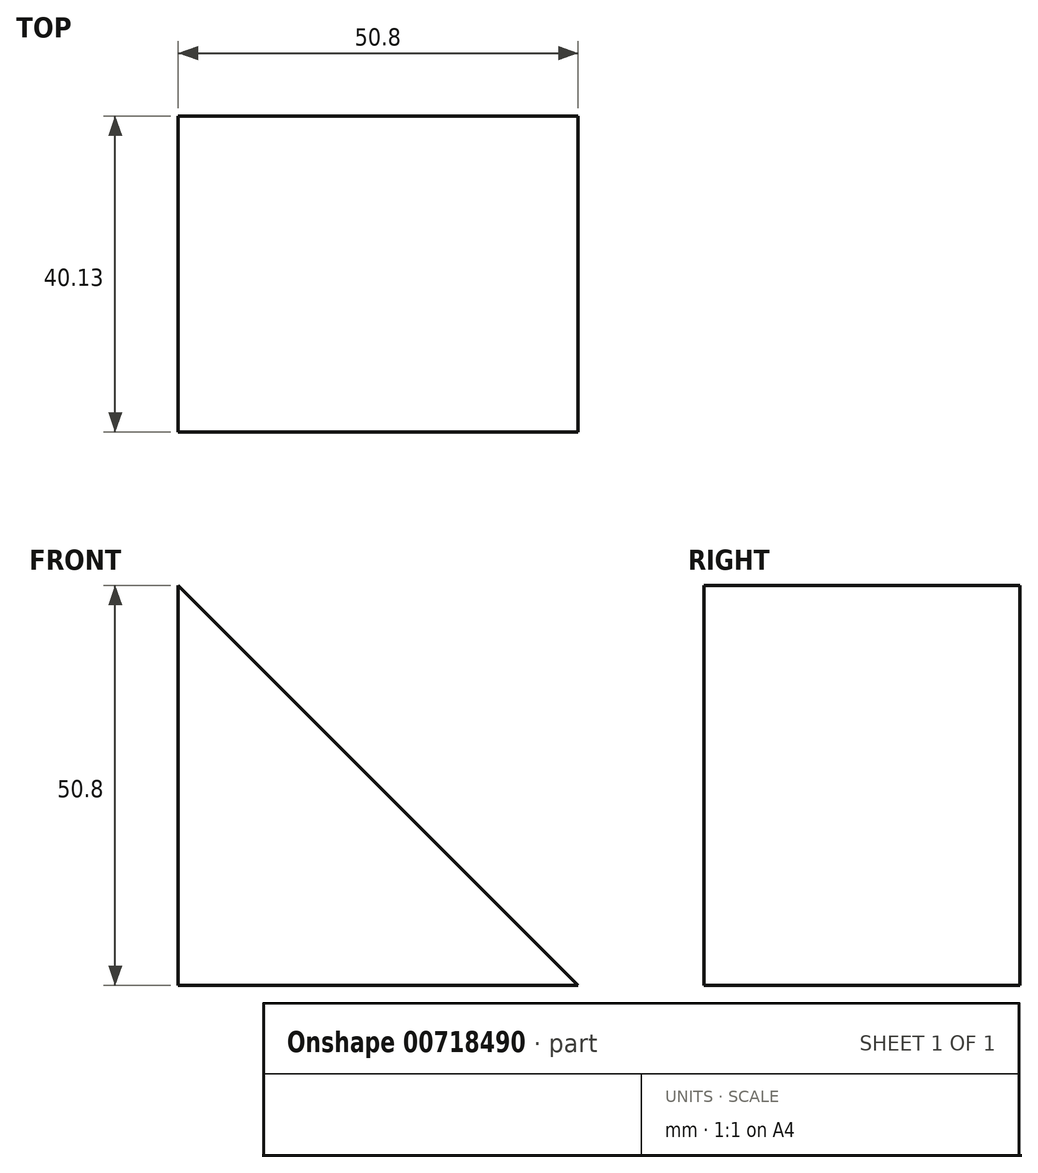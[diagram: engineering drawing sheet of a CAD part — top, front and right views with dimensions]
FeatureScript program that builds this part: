
annotation { "Feature Type Name" : "Feature", "Feature Type Description" : "" }
export const myFeature = defineFeature(function(context is Context, id is Id, definition is map)
    precondition{}
    {
        {
            var Q0;
            Q0=qCreatedBy(makeId("Front.planeOp"),FACE);
            var sketch = newSketch(context, id + "F0", { "sketchPlane" : qUnion([Q0])});
            skLineSegment(sketch, "E0", {"start": v(-43.3, 50.8) * mm, "end": v(-43.3, 0) * mm});
            skLineSegment(sketch, "E1", {"start": v(-43.3, 0) * mm, "end": v(7.5, 0) * mm});
            skLineSegment(sketch, "E2", {"start": v(7.5, 0) * mm, "end": v(-43.3, 50.8) * mm});
            skSolve(sketch);
        }
        {
            var Q0;
            Q0 = qSketchRegion(id + "F0", true);
            extrude(context, id + "F1", {"entities" : qUnion([Q0]), "oppositeDirection" : true, "depth" : 40.13 * mm, "offsetDistance" : 25.4 * mm});
        }
    });
